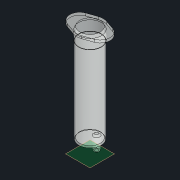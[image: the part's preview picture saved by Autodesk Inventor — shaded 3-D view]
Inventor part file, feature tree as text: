
AUTODESK INVENTOR PART (.ipt)
format: ipt  version: 2022.2 (Build 262287010, 287A)  size: 158,208 bytes
history: native  units: mm
features: sketch x7, extrude x5, plane x1, loft x1, projected_geometry x1
ambient origin geometry x8: Origin, YZ Plane, XZ Plane, XY Plane, X Axis, Y Axis, Z Axis, Center Point
bodies: Solid1 (feature_tree)
feature tree (15):
  extrude  "Extrusion1"  Depth=75.5mm TaperAngle=0.0deg
  extrude  "Extrusion2"  Depth=9.6mm TaperAngle=0.0deg
  extrude  "Extrusion3"  Depth=20.3mm
  extrude  "Extrusion4"  Depth=2.0mm TaperAngle=0.0deg
  sketch  "Sketch5"  dims[d11=15.75mm d12=74.5mm d13=0.0mm]
  plane  "Work Plane1"
  loft  "Loft1"
  extrude  "Extrusion5"  Depth=10.0mm
  sketch  "Sketch1"  dims[d0=17.15mm d1=75.5mm d2=0.0mm]
  sketch  "Sketch2"  dims[d3=17.7mm d4=9.6mm d5=0.0mm]
  sketch  "Sketch3"  dims[d6=20.3mm d7=31.0mm]
  sketch  "Sketch4"  dims[d8=14.3mm d9=2.0mm d10=0.0mm]
  sketch  "Sketch6"  dims[d14=5.0mm d17=10.0mm]
  sketch  "Sketch7"  dims[d18=4.0mm d20=0.0mm d21=90.0deg d22=0.0mm d23=90.0deg d24=0.8mm d25=0.0mm d26=0.0mm]
  projected_geometry  "Projected Loop1"
